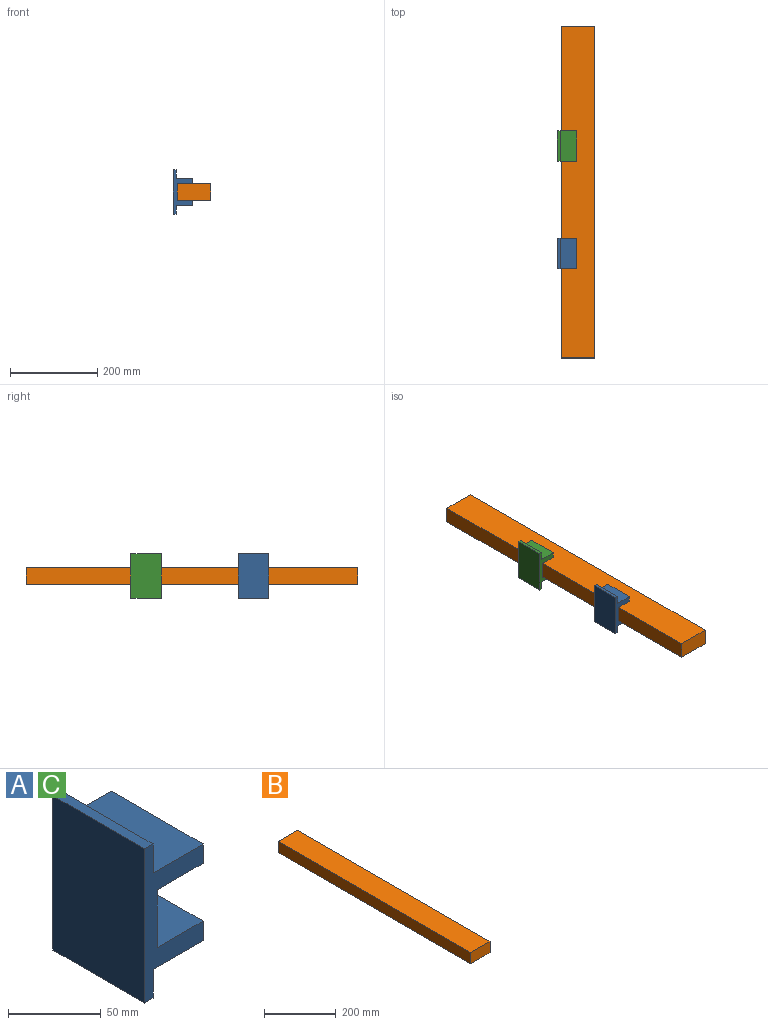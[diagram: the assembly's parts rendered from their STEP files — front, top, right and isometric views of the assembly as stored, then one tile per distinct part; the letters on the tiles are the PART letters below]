
ASSEMBLY  parts=3 mates=2
PART A: 14 faces, bbox 44.5x69.9x101.6 mm
  f0: plane 69.85x38.1mm, normal (0,0,1), area 2661.3mm2, adj f1,f11,f12,f13
  f1: plane 69.85x19.05mm, normal (1,0,0), area 1330.6mm2, adj f0,f2,f12,f13
  f2: plane 69.85x6.35mm, normal (0,0,1), area 443.5mm2, adj f1,f3,f12,f13
  f3: plane 101.6x69.85mm, normal (-1,0,0), area 7096.8mm2, adj f2,f4,f12,f13
  f4: plane 69.85x6.35mm, normal (0,0,-1), area 443.5mm2, adj f3,f5,f12,f13
  f5: plane 69.85x19.05mm, normal (1,0,0), area 1330.6mm2, adj f4,f6,f12,f13
  f6: plane 69.85x38.1mm, normal (0,0,-1), area 2661.3mm2, adj f5,f7,f12,f13
  f7: plane 69.85x12.7mm, normal (1,0,0), area 887.1mm2, adj f6,f8,f12,f13
  f8: plane 69.85x34.93mm, normal (0,0,1), area 2439.5mm2, adj f7,f9,f12,f13
  f9: plane 69.85x38.1mm, normal (1,0,0), area 2661.3mm2, adj f8,f10,f12,f13
  f10: plane 69.85x34.93mm, normal (0,0,-1), area 2439.5mm2, adj f9,f11,f12,f13
  f11: plane 69.85x12.7mm, normal (1,0,0), area 887.1mm2, adj f0,f10,f12,f13
  f12: plane 101.6x44.45mm, normal (0,-1,0), area 1733.9mm2, adj f0,f1,f2,f3,f4,f5,f6,f7
  f13: plane 101.6x44.45mm, normal (0,1,0), area 1733.9mm2, adj f0,f1,f2,f3,f4,f5,f6,f7
PART B: 6 faces, bbox 76.2x762x38.1 mm
  f0: plane 762x76.2mm, normal (0,0,1), area 58064.4mm2, adj f1,f3,f4,f5
  f1: plane 762x38.1mm, normal (-1,0,0), area 29032.2mm2, adj f0,f2,f4,f5
  f2: plane 762x76.2mm, normal (0,0,-1), area 58064.4mm2, adj f1,f3,f4,f5
  f3: plane 762x38.1mm, normal (1,0,0), area 29032.2mm2, adj f0,f2,f4,f5
  f4: plane 76.2x38.1mm, normal (0,-1,0), area 2903.2mm2, adj f0,f1,f2,f3
  f5: plane 76.2x38.1mm, normal (0,1,0), area 2903.2mm2, adj f0,f1,f2,f3
PART C: same geometry as A
PLACE A t=(-110.42,-263.38,-154.42)mm
PLACE B t=(-110.42,224.25,-154.42)mm fixed
PLACE C t=(-110.42,-16.54,-154.42)mm
MATE planar C.f9 <-> B.f1  axis (1,0,0) through (-148.52,-51.47,-135.37)mm
MATE planar A.f9 <-> B.f1  axis (1,0,0) through (-148.52,-298.31,-135.37)mm
